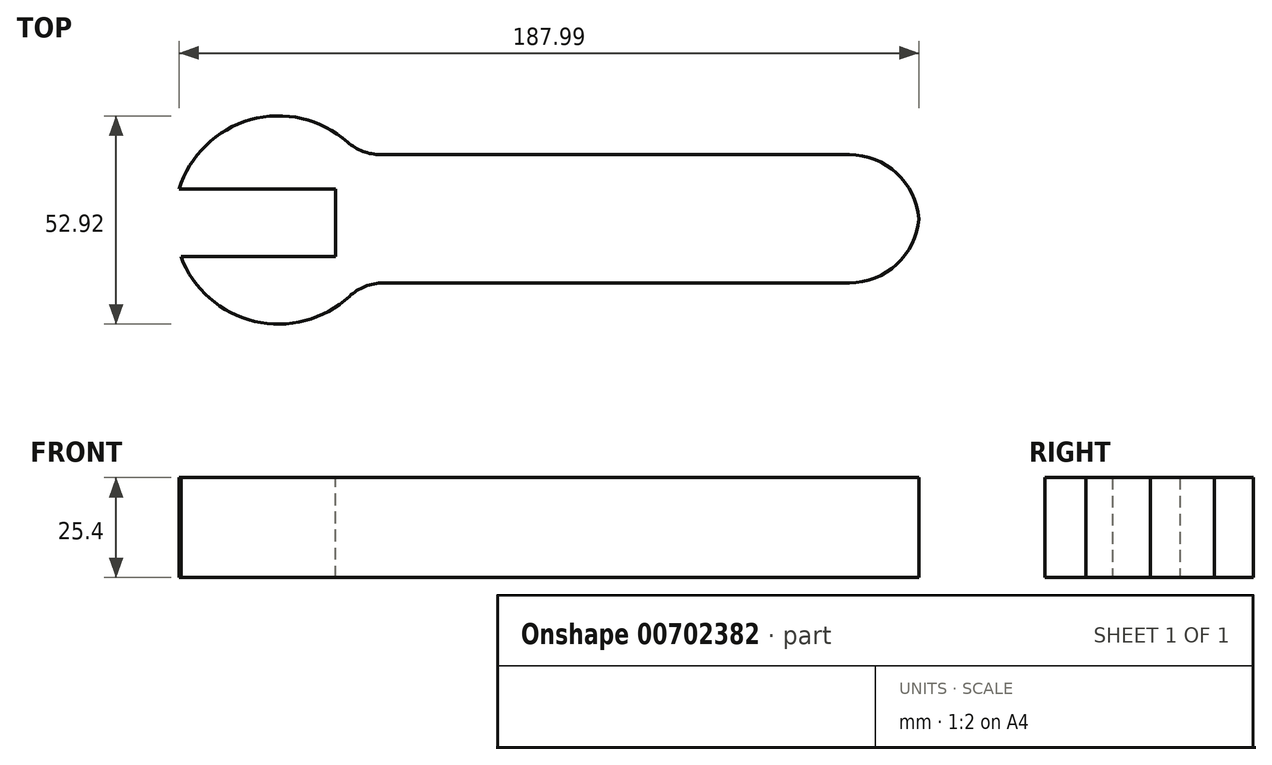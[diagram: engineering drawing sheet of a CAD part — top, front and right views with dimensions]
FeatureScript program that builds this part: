
annotation { "Feature Type Name" : "Feature", "Feature Type Description" : "" }
export const myFeature = defineFeature(function(context is Context, id is Id, definition is map)
    precondition{}
    {
        {
            var Q0;
            Q0=qCreatedBy(makeId("Top.planeOp"),FACE);
            var sketch = newSketch(context, id + "F0", { "sketchPlane" : qUnion([Q0])});
            skLineSegment(sketch, "E0.bottom", {"start": v(-92.23, 16.62) * mm, "end": v(64.97, 16.62) * mm});
            skLineSegment(sketch, "E0.top", {"start": v(-92.23, -16) * mm, "end": v(64.97, -16) * mm});
            skLineSegment(sketch, "E0.left", {"start": v(-92.23, 16.62) * mm, "end": v(-92.23, -16) * mm});
            skLineSegment(sketch, "E0.right", {"start": v(64.97, 16.62) * mm, "end": v(64.97, -16) * mm});
            skCircle(sketch, "E1", {"center": v(-97.8, 0) * mm, "radius": 26.46 * mm});
            skSolve(sketch);
        }
        {
            var Q0;
            Q0=makeQuery(id+"F0.imprint","IMPRINT",FACE,{"disambiguationData":[TD([[makeQuery(id+"F0.imprint","IMPRINT",EDGE,{"derivedFrom":sQuery(id+"F0.wireOp",EDGE,"E0.bottom")}),-1.0]])]});
            var Q1;
            Q1=makeQuery(id+"F0.imprint","IMPRINT",FACE,{"disambiguationData":[TD([[makeQuery(id+"F0.imprint","IMPRINT",EDGE,{"derivedFrom":sQuery(id+"F0.wireOp",EDGE,"E1")}),1.0]])]});
            extrude(context, id + "F1", {"entities" : qUnion([Q0, Q1]), "depth" : 25.4 * mm, "offsetDistance" : 25.4 * mm});
        }
        {
            var Q0;
            Q0=makeQuery(id+"F1.opExtrude","CAP_FACE",FACE,{"disambiguationData":[OSD([sQuery(id+"F0.wireOp",EDGE,"E0.bottom"),sQuery(id+"F0.wireOp",EDGE,"E0.top"),sQuery(id+"F0.wireOp",EDGE,"E0.right"),sQuery(id+"F0.wireOp",EDGE,"E1")])],"isStart":false});
            var sketch = newSketch(context, id + "F2", { "sketchPlane" : qUnion([Q0])});
            skLineSegment(sketch, "E2.bottom", {"start": v(-131.84, 7.85) * mm, "end": v(-83.35, 7.85) * mm});
            skLineSegment(sketch, "E2.top", {"start": v(-131.84, -9.25) * mm, "end": v(-83.35, -9.25) * mm});
            skLineSegment(sketch, "E2.left", {"start": v(-131.84, 7.85) * mm, "end": v(-131.84, -9.25) * mm});
            skLineSegment(sketch, "E2.right", {"start": v(-83.35, 7.85) * mm, "end": v(-83.35, -9.25) * mm});
            skSolve(sketch);
        }
        {
            var Q0;
            {var subQ0=sQuery(id+"F2.wireOp",EDGE,"E2.right");Q0=makeQuery(id+"F2.imprint","IMPRINT",FACE,{"disambiguationData":[TD([[makeQuery(id+"F2.imprint","IMPRINT",EDGE,{"derivedFrom":subQ0}),-1.0]])]});}
            var Q1;
            {var subQ0=sQuery(id+"F2.wireOp",EDGE,"E2.left");Q1=makeQuery(id+"F2.imprint","IMPRINT",FACE,{"disambiguationData":[TD([[makeQuery(id+"F2.imprint","IMPRINT",EDGE,{"derivedFrom":subQ0}),1.0]])]});}
            extrude(context, id + "F3", {"entities" : qUnion([Q0, Q1]), "operationType" : NewBodyOperationType.REMOVE, "oppositeDirection" : true, "depth" : 38.1 * mm, "offsetDistance" : 25.4 * mm});
        }
        {
            var Q0;
            Q0=makeQuery(id+"F1.opExtrude","SWEPT_EDGE",EDGE,{"disambiguationData":[OSD([sQuery(id+"F0.wireOp",EDGE,"E0.bottom"),sQuery(id+"F0.wireOp",EDGE,"E1")])]});
            fillet(context, id + "F4", {"entities" : qUnion([Q0]), "radius" : 12.7 * mm, "tangentPropagation" : true, "allowEdgeOverflow" : false});
        }
        {
            var Q0;
            Q0=makeQuery(id+"F1.opExtrude","SWEPT_EDGE",EDGE,{"disambiguationData":[OSD([sQuery(id+"F0.wireOp",EDGE,"E0.top"),sQuery(id+"F0.wireOp",EDGE,"E1")])]});
            fillet(context, id + "F5", {"entities" : qUnion([Q0]), "radius" : 12.7 * mm, "tangentPropagation" : true, "allowEdgeOverflow" : false});
        }
        {
            var Q0;
            Q0=makeQuery(id+"F1.opExtrude","SWEPT_EDGE",EDGE,{"disambiguationData":[OSD([sQuery(id+"F0.wireOp",EDGE,"E0.bottom"),sQuery(id+"F0.wireOp",EDGE,"E0.right")])]});
            var Q1;
            Q1=makeQuery(id+"F1.opExtrude","SWEPT_EDGE",EDGE,{"disambiguationData":[OSD([sQuery(id+"F0.wireOp",EDGE,"E0.top"),sQuery(id+"F0.wireOp",EDGE,"E0.right")])]});
            fillet(context, id + "F6", {"entities" : qUnion([Q0, Q1]), "radius" : 17.78 * mm, "tangentPropagation" : true, "allowEdgeOverflow" : false});
        }
    });
